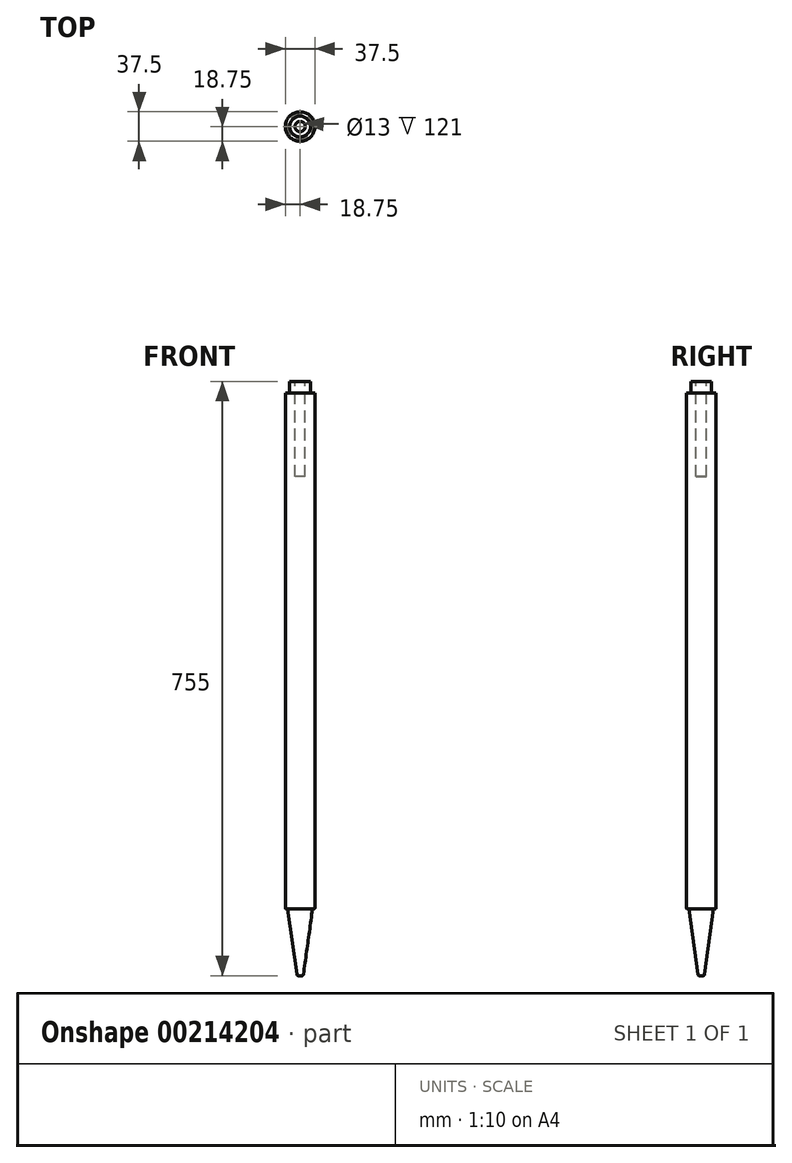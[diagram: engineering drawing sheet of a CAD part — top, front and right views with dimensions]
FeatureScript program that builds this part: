
annotation { "Feature Type Name" : "Feature", "Feature Type Description" : "" }
export const myFeature = defineFeature(function(context is Context, id is Id, definition is map)
    precondition{}
    {
        {
            var Q0;
            Q0=qCreatedBy(makeId("Front.planeOp"),FACE);
            var sketch = newSketch(context, id + "F0", { "sketchPlane" : qUnion([Q0])});
            skLineSegment(sketch, "E0", {"start": v(0, 216.86) * mm, "end": v(0, -155.63) * mm, "construction": true});
            skLineSegment(sketch, "E1", {"start": v(-13.25, 740) * mm, "end": v(-18.75, 740) * mm});
            skLineSegment(sketch, "E2", {"start": v(-18.75, 740) * mm, "end": v(-18.75, 86) * mm});
            skLineSegment(sketch, "E3", {"start": v(-17.75, 85) * mm, "end": v(-15.75, 85) * mm});
            skLineSegment(sketch, "E4", {"start": v(-15.75, 85) * mm, "end": v(-4.24, 1.73) * mm});
            skLineSegment(sketch, "E5", {"start": v(-2.26, 0) * mm, "end": v(0, 0) * mm});
            skLineSegment(sketch, "E6", {"start": v(-13.25, 755) * mm, "end": v(-13.25, 740) * mm});
            skLineSegment(sketch, "E7", {"start": v(-13.25, 755) * mm, "end": v(-6.5, 755) * mm});
            skLineSegment(sketch, "E8", {"start": v(-6.5, 755) * mm, "end": v(-6.5, 634) * mm});
            skLineSegment(sketch, "E9", {"start": v(-6.5, 634) * mm, "end": v(0, 634) * mm});
            skLineSegment(sketch, "E10", {"start": v(0, 634) * mm, "end": v(0, 0) * mm});
            skPoint(sketch, "E11.visualSharp", {"position": v(-4, 0) * mm});
            skArc(sketch, "E11.filletArc", {"start": v(-4.24, 1.73) * mm, "mid": v(-3.57, 0.5) * mm, "end": v(-2.26, 0) * mm});
            skPoint(sketch, "E12.visualSharp", {"position": v(-18.75, 85) * mm});
            skArc(sketch, "E12.filletArc", {"start": v(-18.75, 86) * mm, "mid": v(-18.46, 85.3) * mm, "end": v(-17.75, 85) * mm});
            skLineSegment(sketch, "E13", {"start": v(-42.39, 796) * mm, "end": v(43.6, 796) * mm, "construction": true});
            skSolve(sketch);
        }
        {
            var Q0;
            Q0=makeQuery(id+"F0.imprint","IMPRINT",FACE,{"disambiguationData":[TD([[makeQuery(id+"F0.imprint","IMPRINT",EDGE,{"derivedFrom":sQuery(id+"F0.wireOp",EDGE,"E1")}),1.0]])]});
            var Q1;
            Q1=sQuery(id+"F0.wireOp",EDGE,"E10");
            revolve(context, id + "F1", {"entities" : qUnion([Q0]), "axis" : qUnion([Q1]), "revolveType" : RevolveType.FULL});
        }
    });
